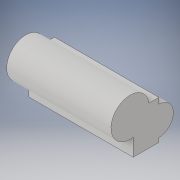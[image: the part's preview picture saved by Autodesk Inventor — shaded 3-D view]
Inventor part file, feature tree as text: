
AUTODESK INVENTOR PART (.ipt)
format: ipt  version: 2017 SP1 (Build 210196100, 196)  size: 98,304 bytes
history: native  units: in
note: dims shown in document units (in); Inventor stores cm internally (conversion verified against a paired STEP export)
features: other x1, extrude x1, sketch x1
ambient origin geometry x8: Origin, YZ Plane, XZ Plane, XY Plane, X Axis, Y Axis, Z Axis, Center Point
bodies: Solid1 (feature_tree)
feature tree (3):
  other  "test"
  extrude  "Extrusion1"  [1 undecoded]
  sketch  "Sketch1"  dims[d0=2.0in d1=0.0in]
note: 1 required parameter value undecoded (feature->parameter linkage not recoverable at this tier; creation-order binding heuristic only, values carry confidence <= 0.55)
